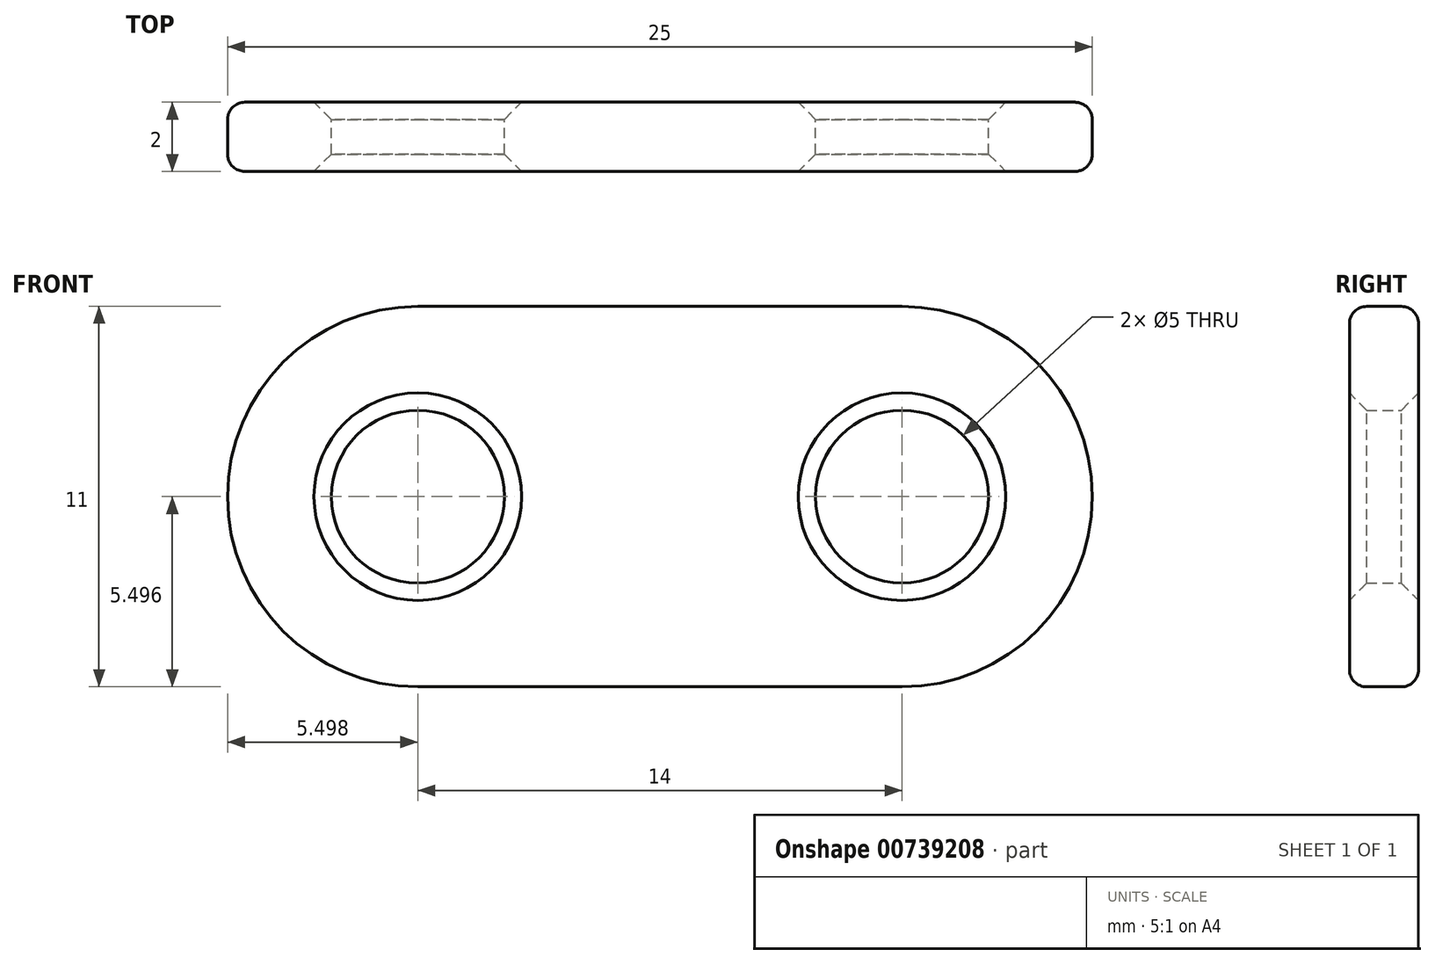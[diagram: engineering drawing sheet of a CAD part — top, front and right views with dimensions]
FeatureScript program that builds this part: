
annotation { "Feature Type Name" : "Feature", "Feature Type Description" : "" }
export const myFeature = defineFeature(function(context is Context, id is Id, definition is map)
    precondition{}
    {
        {
            var Q0;
            Q0=qCreatedBy(makeId("Front.planeOp"),FACE);
            var sketch = newSketch(context, id + "F0", { "sketchPlane" : qUnion([Q0])});
            skLineSegment(sketch, "E0", {"start": v(-23.86, 18.23) * mm, "end": v(-9.86, 18.23) * mm});
            skLineSegment(sketch, "E1", {"start": v(-23.86, 7.23) * mm, "end": v(-9.86, 7.23) * mm});
            skArc(sketch, "E2", {"start": v(-23.86, 18.23) * mm, "mid": v(-29.36, 12.73) * mm, "end": v(-23.86, 7.23) * mm});
            skArc(sketch, "E3", {"start": v(-9.86, 7.23) * mm, "mid": v(-4.36, 12.73) * mm, "end": v(-9.86, 18.23) * mm});
            skCircle(sketch, "E4", {"center": v(-9.86, 12.73) * mm, "radius": 2.5 * mm});
            skCircle(sketch, "E5", {"center": v(-23.86, 12.73) * mm, "radius": 2.5 * mm});
            skSolve(sketch);
        }
        {
            var Q0;
            Q0 = qSketchRegion(id + "F0", true);
            extrude(context, id + "F1", {"entities" : qUnion([Q0]), "depth" : 2 * mm, "offsetDistance" : 25.4 * mm});
        }
        {
            var Q0;
            Q0=makeQuery(id+"F1.opExtrude","CAP_EDGE",EDGE,{"disambiguationData":[OSD([sQuery(id+"F0.wireOp",EDGE,"E5")])],"isStart":false});
            var Q1;
            Q1=makeQuery(id+"F1.opExtrude","CAP_EDGE",EDGE,{"disambiguationData":[OSD([sQuery(id+"F0.wireOp",EDGE,"E5")])],"isStart":true});
            var Q2;
            Q2=makeQuery(id+"F1.opExtrude","CAP_EDGE",EDGE,{"disambiguationData":[OSD([sQuery(id+"F0.wireOp",EDGE,"E4")])],"isStart":false});
            var Q3;
            Q3=makeQuery(id+"F1.opExtrude","CAP_EDGE",EDGE,{"disambiguationData":[OSD([sQuery(id+"F0.wireOp",EDGE,"E4")])],"isStart":true});
            chamfer(context, id + "F2", {"entities" : qUnion([Q0, Q1, Q2, Q3]), "width" : 0.5 * mm, "tangentPropagation" : true});
        }
        {
            var Q0;
            Q0=makeQuery(id+"F1.opExtrude","CAP_EDGE",EDGE,{"disambiguationData":[OSD([sQuery(id+"F0.wireOp",EDGE,"E1")])],"isStart":false});
            var Q1;
            Q1=makeQuery(id+"F1.opExtrude","CAP_EDGE",EDGE,{"disambiguationData":[OSD([sQuery(id+"F0.wireOp",EDGE,"E2")])],"isStart":true});
            fillet(context, id + "F3", {"entities" : qUnion([Q0, Q1]), "radius" : 0.5 * mm, "tangentPropagation" : true, "allowEdgeOverflow" : false});
        }
    });
